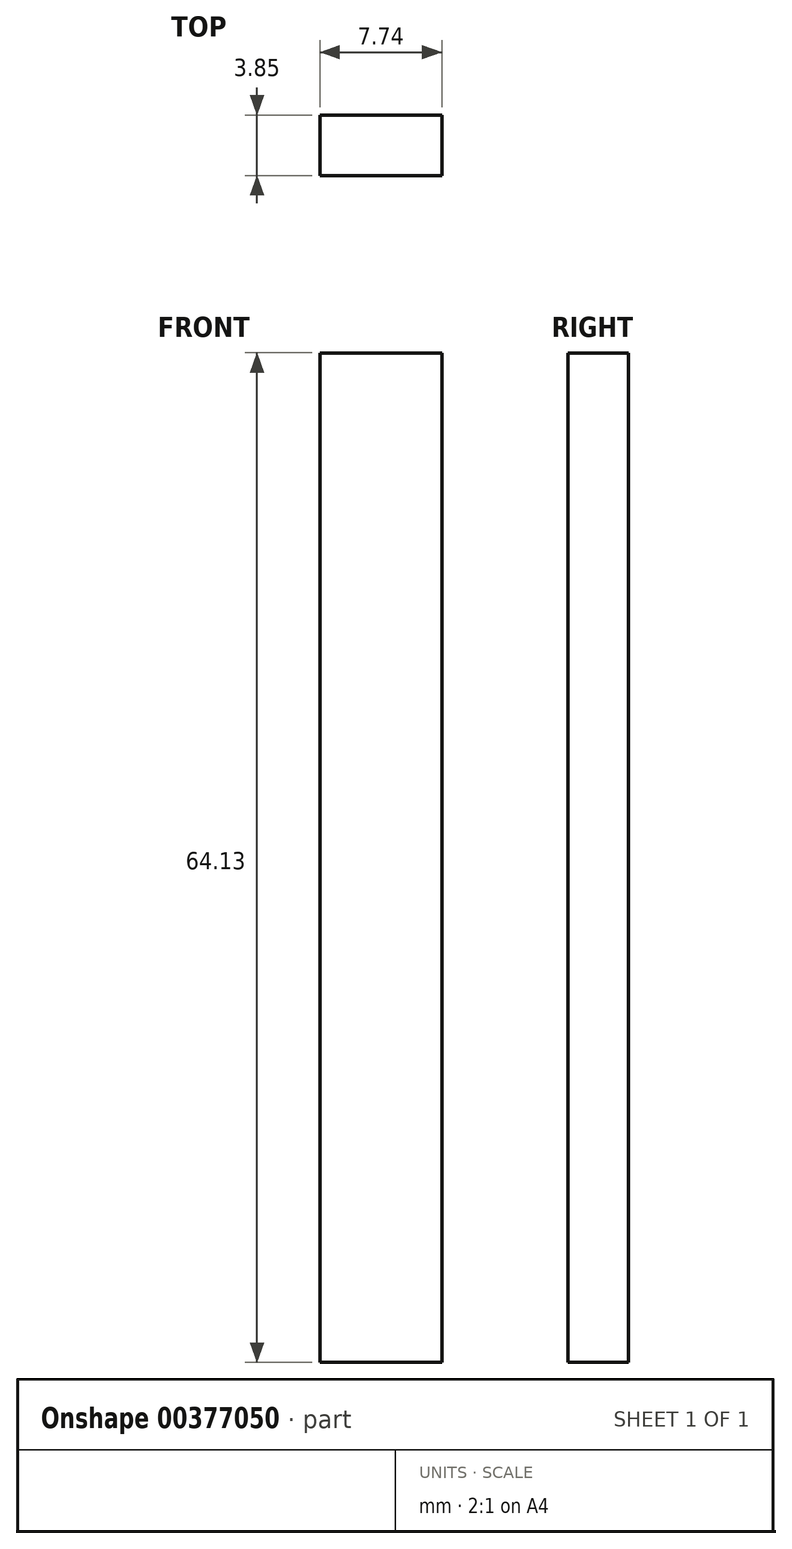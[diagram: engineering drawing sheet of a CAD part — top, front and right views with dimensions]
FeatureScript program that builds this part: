
annotation { "Feature Type Name" : "Feature", "Feature Type Description" : "" }
export const myFeature = defineFeature(function(context is Context, id is Id, definition is map)
    precondition{}
    {
        {
            var Q0;
            Q0=qCreatedBy(makeId("Right.planeOp"),FACE);
            var sketch = newSketch(context, id + "F0", { "sketchPlane" : qUnion([Q0])});
            skLineSegment(sketch, "E0.bottom", {"start": v(-22.8, 64.13) * mm, "end": v(-26.66, 64.13) * mm});
            skLineSegment(sketch, "E0.top", {"start": v(-22.8, 0) * mm, "end": v(-26.66, 0) * mm});
            skLineSegment(sketch, "E0.left", {"start": v(-22.8, 64.13) * mm, "end": v(-22.8, 0) * mm});
            skLineSegment(sketch, "E0.right", {"start": v(-26.66, 64.13) * mm, "end": v(-26.66, 0) * mm});
            skSolve(sketch);
        }
        {
            var Q0;
            Q0=makeQuery(id+"F0.imprint","IMPRINT",FACE,{"disambiguationData":[TD([[makeQuery(id+"F0.imprint","IMPRINT",EDGE,{"derivedFrom":sQuery(id+"F0.wireOp",EDGE,"E0.bottom")}),1.0]])]});
            extrude(context, id + "F1", {"entities" : qUnion([Q0]), "depth" : 7.74 * mm});
        }
    });
